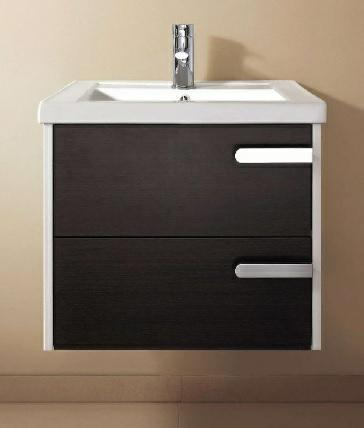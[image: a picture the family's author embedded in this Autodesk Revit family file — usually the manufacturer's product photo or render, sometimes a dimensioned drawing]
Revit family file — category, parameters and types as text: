
# Revit family: FS2011006
name_source: partatom
category: Plumbing Fixtures
revit_build: Autodesk Revit 2016 (Build: 20150220_1215(x64)
units: mm (PartAtom-declared; Revit-internal decimal feet)

## family parameters
Always vertical = Yes
Cut with Voids When Loaded = No
Host = Wall
OmniClass Number = 23.45.00.00
OmniClass Title = Sanitary, Laundry, and Cleaning Equipment
Part Type = Normal
Room Calculation Point = No
Round Connector Dimension = Use Diameter
Shared = No

## types (1)
- 600
    Assembly Code = D2010310
    CW Connection = Yes
    Casework Material = Plastic, White
    Cover Material = Porcelain, Ivory
    Depth = 465 mm
    Description = Mueble de baño 60 x 46 x 52 cm. Incluye lavabo. Color Wengue + Blanco
    Drawer Material = Birch
    HW Connection = Yes
    Handle Material = Stainless Steel, Brushed
    Height = 820 mm
    Manufacturer = CHC
    Model = FS2011005
    Type Image = FS2011005.jpg
    URL = www.grupochc.cl
    Vent Connection = No
    Waste Connection = Yes
    Width = 600 mm

## geometry (parser evidence)
native form markers: Sweep x2
no freeform markers — native parametric forms only
